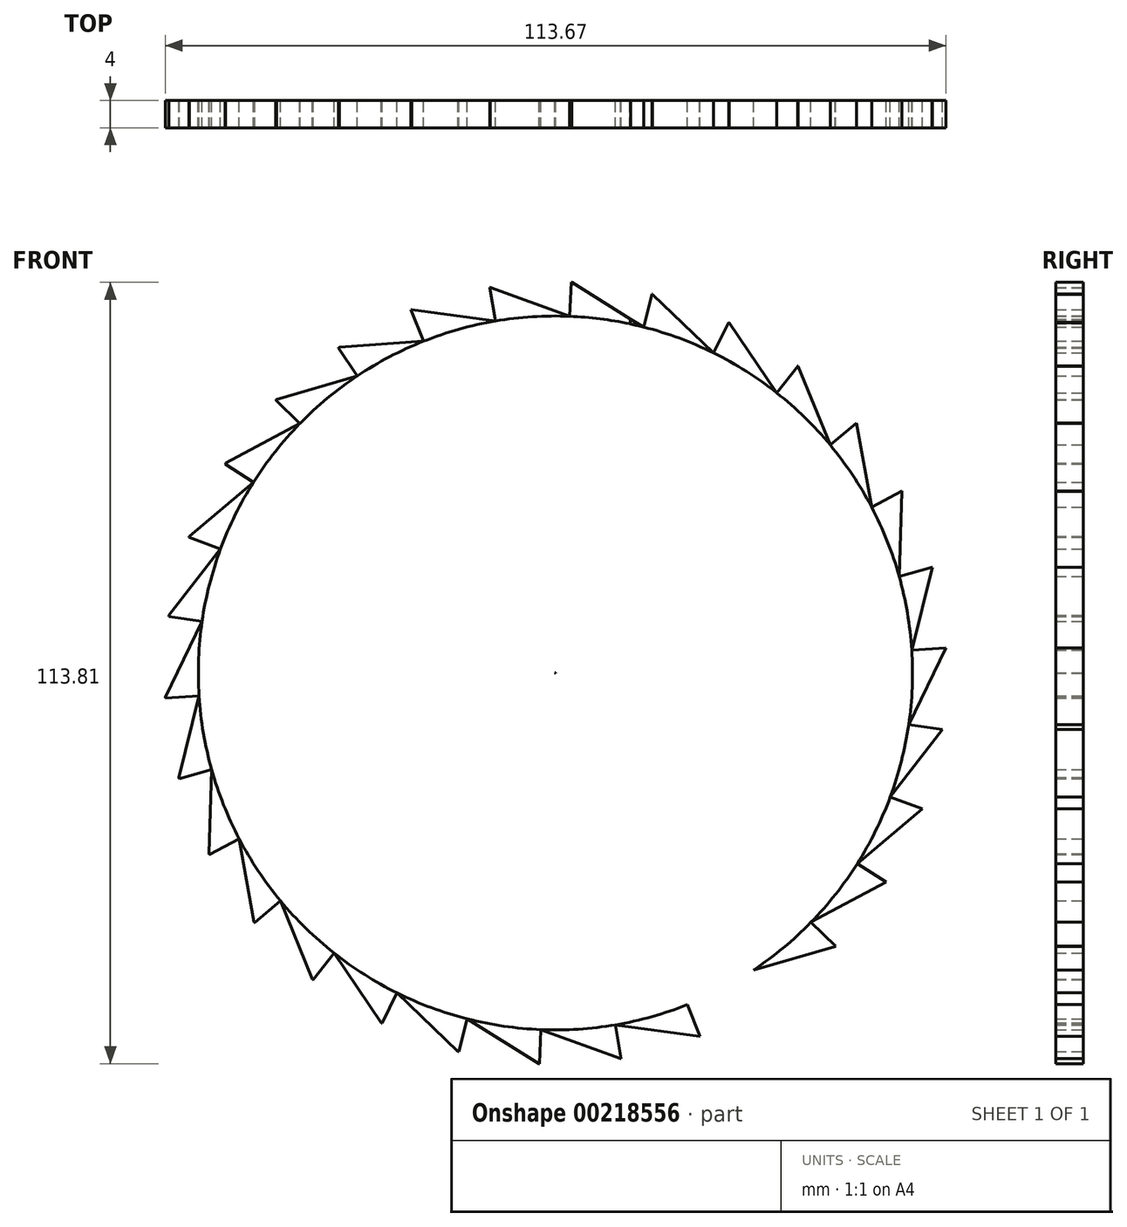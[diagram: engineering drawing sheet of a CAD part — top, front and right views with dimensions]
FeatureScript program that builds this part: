
annotation { "Feature Type Name" : "Feature", "Feature Type Description" : "" }
export const myFeature = defineFeature(function(context is Context, id is Id, definition is map)
    precondition{}
    {
        {
            var Q0;
            Q0=qCreatedBy(makeId("Front.planeOp"),FACE);
            var sketch = newSketch(context, id + "F0", { "sketchPlane" : qUnion([Q0])});
            skLineSegment(sketch, "E0", {"start": v(16.93, -54.43) * mm, "end": v(16.97, -54.42) * mm});
            skPoint(sketch, "E1.center", {"position": v(-0.03, 0) * mm});
            skCircle(sketch, "E2", {"center": v(-0.03, 0) * mm, "radius": 52 * mm});
            skLineSegment(sketch, "E3", {"start": v(0, 0) * mm, "end": v(-0.03, 0) * mm});
            skLineSegment(sketch, "E4", {"start": v(48.74, -18.05) * mm, "end": v(53.43, -19.79) * mm});
            skLineSegment(sketch, "E5", {"start": v(53.43, -19.79) * mm, "end": v(43.92, -27.8) * mm});
            skLineSegment(sketch, "E6.1.0", {"start": v(43.92, -27.8) * mm, "end": v(48.14, -30.47) * mm});
            skLineSegment(sketch, "E6.1.1", {"start": v(48.14, -30.47) * mm, "end": v(37.18, -36.33) * mm});
            skLineSegment(sketch, "E6.2.0", {"start": v(37.18, -36.33) * mm, "end": v(40.76, -39.82) * mm});
            skLineSegment(sketch, "E6.2.1", {"start": v(40.76, -39.82) * mm, "end": v(28.81, -43.27) * mm});
            skLineSegment(sketch, "E6.3.0", {"start": v(28.81, -43.27) * mm, "end": v(31.59, -47.43) * mm});
            skLineSegment(sketch, "E6.3.1", {"start": v(31.59, -47.43) * mm, "end": v(19.18, -48.32) * mm});
            skLineSegment(sketch, "E6.4.0", {"start": v(19.19, -48.32) * mm, "end": v(21.03, -52.96) * mm});
            skLineSegment(sketch, "E6.4.1", {"start": v(21.03, -52.96) * mm, "end": v(8.72, -51.26) * mm});
            skLineSegment(sketch, "E6.5.0", {"start": v(8.72, -51.26) * mm, "end": v(9.56, -56.19) * mm});
            skLineSegment(sketch, "E6.5.1", {"start": v(9.56, -56.19) * mm, "end": v(-2.13, -51.96) * mm});
            skLineSegment(sketch, "E6.6.0", {"start": v(-2.13, -51.96) * mm, "end": v(-2.33, -56.95) * mm});
            skLineSegment(sketch, "E6.6.1", {"start": v(-2.33, -56.95) * mm, "end": v(-12.89, -50.39) * mm});
            skLineSegment(sketch, "E6.7.0", {"start": v(-12.88, -50.39) * mm, "end": v(-14.12, -55.23) * mm});
            skLineSegment(sketch, "E6.7.1", {"start": v(-14.12, -55.23) * mm, "end": v(-23.08, -46.61) * mm});
            skLineSegment(sketch, "E6.8.0", {"start": v(-23.08, -46.61) * mm, "end": v(-25.3, -51.1) * mm});
            skLineSegment(sketch, "E6.8.1", {"start": v(-25.3, -51.1) * mm, "end": v(-32.27, -40.8) * mm});
            skLineSegment(sketch, "E6.9.0", {"start": v(-32.27, -40.8) * mm, "end": v(-35.37, -44.72) * mm});
            skLineSegment(sketch, "E6.9.1", {"start": v(-35.37, -44.72) * mm, "end": v(-40.05, -33.2) * mm});
            skLineSegment(sketch, "E6.10.0", {"start": v(-40.05, -33.2) * mm, "end": v(-43.9, -36.4) * mm});
            skLineSegment(sketch, "E6.10.1", {"start": v(-43.9, -36.4) * mm, "end": v(-46.08, -24.16) * mm});
            skLineSegment(sketch, "E6.11.0", {"start": v(-46.08, -24.16) * mm, "end": v(-50.5, -26.49) * mm});
            skLineSegment(sketch, "E6.11.1", {"start": v(-50.5, -26.49) * mm, "end": v(-50.1, -14.06) * mm});
            skLineSegment(sketch, "E6.12.0", {"start": v(-50.1, -14.06) * mm, "end": v(-54.9, -15.41) * mm});
            skLineSegment(sketch, "E6.12.1", {"start": v(-54.9, -15.41) * mm, "end": v(-51.92, -3.34) * mm});
            skLineSegment(sketch, "E6.13.0", {"start": v(-51.92, -3.34) * mm, "end": v(-56.91, -3.67) * mm});
            skLineSegment(sketch, "E6.13.1", {"start": v(-56.91, -3.67) * mm, "end": v(-51.48, 7.52) * mm});
            skLineSegment(sketch, "E6.14.0", {"start": v(-51.48, 7.52) * mm, "end": v(-56.43, 8.24) * mm});
            skLineSegment(sketch, "E6.14.1", {"start": v(-56.43, 8.24) * mm, "end": v(-48.8, 18.05) * mm});
            skLineSegment(sketch, "E6.15.0", {"start": v(-48.8, 18.05) * mm, "end": v(-53.49, 19.79) * mm});
            skLineSegment(sketch, "E6.15.1", {"start": v(-53.49, 19.79) * mm, "end": v(-43.98, 27.8) * mm});
            skLineSegment(sketch, "E6.16.0", {"start": v(-43.98, 27.8) * mm, "end": v(-48.2, 30.47) * mm});
            skLineSegment(sketch, "E6.16.1", {"start": v(-48.2, 30.47) * mm, "end": v(-37.24, 36.33) * mm});
            skLineSegment(sketch, "E6.17.0", {"start": v(-37.24, 36.33) * mm, "end": v(-40.82, 39.82) * mm});
            skLineSegment(sketch, "E6.17.1", {"start": v(-40.82, 39.82) * mm, "end": v(-28.87, 43.27) * mm});
            skLineSegment(sketch, "E6.18.0", {"start": v(-28.87, 43.27) * mm, "end": v(-31.65, 47.43) * mm});
            skLineSegment(sketch, "E6.18.1", {"start": v(-31.65, 47.43) * mm, "end": v(-19.24, 48.32) * mm});
            skLineSegment(sketch, "E6.19.0", {"start": v(-19.25, 48.32) * mm, "end": v(-21.1, 52.96) * mm});
            skLineSegment(sketch, "E6.19.1", {"start": v(-21.1, 52.96) * mm, "end": v(-8.78, 51.26) * mm});
            skLineSegment(sketch, "E6.20.0", {"start": v(-8.78, 51.26) * mm, "end": v(-9.62, 56.19) * mm});
            skLineSegment(sketch, "E6.20.1", {"start": v(-9.62, 56.19) * mm, "end": v(2.07, 51.96) * mm});
            skLineSegment(sketch, "E6.21.0", {"start": v(2.07, 51.96) * mm, "end": v(2.27, 56.95) * mm});
            skLineSegment(sketch, "E6.21.1", {"start": v(2.27, 56.95) * mm, "end": v(12.83, 50.39) * mm});
            skLineSegment(sketch, "E6.22.0", {"start": v(12.82, 50.39) * mm, "end": v(14.06, 55.23) * mm});
            skLineSegment(sketch, "E6.22.1", {"start": v(14.06, 55.23) * mm, "end": v(23.02, 46.61) * mm});
            skLineSegment(sketch, "E6.23.0", {"start": v(23.02, 46.61) * mm, "end": v(25.24, 51.1) * mm});
            skLineSegment(sketch, "E6.23.1", {"start": v(25.24, 51.1) * mm, "end": v(32.2, 40.8) * mm});
            skLineSegment(sketch, "E6.24.0", {"start": v(32.2, 40.8) * mm, "end": v(35.3, 44.72) * mm});
            skLineSegment(sketch, "E6.24.1", {"start": v(35.3, 44.72) * mm, "end": v(39.99, 33.2) * mm});
            skLineSegment(sketch, "E6.25.0", {"start": v(39.99, 33.2) * mm, "end": v(43.83, 36.4) * mm});
            skLineSegment(sketch, "E6.25.1", {"start": v(43.83, 36.4) * mm, "end": v(46.02, 24.16) * mm});
            skLineSegment(sketch, "E6.26.0", {"start": v(46.02, 24.16) * mm, "end": v(50.44, 26.49) * mm});
            skLineSegment(sketch, "E6.26.1", {"start": v(50.44, 26.49) * mm, "end": v(50.03, 14.06) * mm});
            skLineSegment(sketch, "E6.27.0", {"start": v(50.03, 14.06) * mm, "end": v(54.85, 15.41) * mm});
            skLineSegment(sketch, "E6.27.1", {"start": v(54.85, 15.41) * mm, "end": v(51.86, 3.34) * mm});
            skLineSegment(sketch, "E6.28.0", {"start": v(51.86, 3.34) * mm, "end": v(56.85, 3.67) * mm});
            skLineSegment(sketch, "E6.28.1", {"start": v(56.85, 3.67) * mm, "end": v(51.42, -7.52) * mm});
            skLineSegment(sketch, "E6.29.0", {"start": v(51.42, -7.52) * mm, "end": v(56.37, -8.24) * mm});
            skLineSegment(sketch, "E6.29.1", {"start": v(56.37, -8.24) * mm, "end": v(48.74, -18.05) * mm});
            skLineSegment(sketch, "E7", {"start": v(30.07, -45.16) * mm, "end": v(31.59, -47.43) * mm});
            skPoint(sketch, "E8.visualSharp", {"position": v(33.26, -42.81) * mm});
            skArc(sketch, "E8.filletArc", {"start": v(33.31, -42.89) * mm, "mid": v(33.25, -42.83) * mm, "end": v(33.17, -42.8) * mm});
            skPoint(sketch, "E9.visualSharp", {"position": v(30.65, -45.05) * mm});
            skLineSegment(sketch, "E10", {"start": v(-0.03, 0) * mm, "end": v(0, 0.04) * mm});
            skArc(sketch, "E11", {"start": v(35.3, 44.72) * mm, "mid": v(35.3, 44.73) * mm, "end": v(35.3, 44.73) * mm});
            skLineSegment(sketch, "E12", {"start": v(32.2, 40.8) * mm, "end": v(32.2, 40.82) * mm});
            skLineSegment(sketch, "E13.trimOffspring", {"start": v(32.2, 40.8) * mm, "end": v(35.3, 44.73) * mm});
            skArc(sketch, "E14", {"start": v(-8.23, 38.75) * mm, "mid": v(-28, 28) * mm, "end": v(-38.72, 8.22) * mm});
            skCircle(sketch, "E15", {"center": v(0, 0.04) * mm, "radius": 1.5 * mm});
            skArc(sketch, "E16", {"start": v(-4.9, -1) * mm, "mid": v(-3.54, -3.5) * mm, "end": v(-1.04, -4.85) * mm});
            skLineSegment(sketch, "E17", {"start": v(0, 52) * mm, "end": v(0, 52.7) * mm, "construction": true});
            skLineSegment(sketch, "E18", {"start": v(-1.04, 4.93) * mm, "end": v(-8.23, 38.75) * mm});
            skLineSegment(sketch, "E19", {"start": v(1.04, 4.93) * mm, "end": v(8.23, 38.75) * mm});
            skLineSegment(sketch, "E20.trimOffspring", {"start": v(10.8, 50.86) * mm, "end": v(10.95, 51.55) * mm});
            skPoint(sketch, "E21.orphan", {"position": v(0, 5.04) * mm});
            skLineSegment(sketch, "E22", {"start": v(0, 0.04) * mm, "end": v(0, 0) * mm});
            skLineSegment(sketch, "E23", {"start": v(-38.72, 8.22) * mm, "end": v(-4.9, 1.04) * mm});
            skLineSegment(sketch, "E24", {"start": v(0, 0.04) * mm, "end": v(-0.1, 0.02) * mm});
            skLineSegment(sketch, "E25", {"start": v(0, 0) * mm, "end": v(0, 0) * mm});
            skLineSegment(sketch, "E26.trimOffspring", {"start": v(-0.1, 0.02) * mm, "end": v(0, 0) * mm});
            skLineSegment(sketch, "E27.trimOffspring", {"start": v(-4.9, -1) * mm, "end": v(-38.71, -8.2) * mm});
            skLineSegment(sketch, "E28.trimOffspring", {"start": v(4.9, 1.04) * mm, "end": v(38.72, 8.23) * mm});
            skLineSegment(sketch, "E29.trimOffspring", {"start": v(4.88, -1.04) * mm, "end": v(38.7, -8.23) * mm});
            skLineSegment(sketch, "E30.trimOffspring", {"start": v(1.04, -4.85) * mm, "end": v(8.23, -38.67) * mm});
            skLineSegment(sketch, "E31.trimOffspring", {"start": v(-1.04, -4.85) * mm, "end": v(-8.23, -38.67) * mm});
            skArc(sketch, "E32.trimOffspring", {"start": v(-1.04, 4.93) * mm, "mid": v(-3.55, 3.56) * mm, "end": v(-4.9, 1.04) * mm});
            skArc(sketch, "E33.trimOffspring", {"start": v(4.9, 1.04) * mm, "mid": v(3.55, 3.56) * mm, "end": v(1.04, 4.93) * mm});
            skArc(sketch, "E34.trimOffspring", {"start": v(1.04, -4.85) * mm, "mid": v(3.52, -3.51) * mm, "end": v(4.88, -1.04) * mm});
            skArc(sketch, "E35.trimOffspring", {"start": v(38.72, 8.23) * mm, "mid": v(28, 28.01) * mm, "end": v(8.23, 38.75) * mm});
            skArc(sketch, "E36.trimOffspring", {"start": v(8.23, -38.67) * mm, "mid": v(27.97, -27.96) * mm, "end": v(38.7, -8.23) * mm});
            skArc(sketch, "E37.trimOffspring", {"start": v(-38.71, -8.2) * mm, "mid": v(-27.99, -27.95) * mm, "end": v(-8.23, -38.67) * mm});
            skCircle(sketch, "E38", {"center": v(0, 0) * mm, "radius": 56.95 * mm});
            skSolve(sketch);
        }
        {
            var Q0;
            {var subQ0=sQuery(id+"F0.wireOp",EDGE,"E5");var subQ1=sQuery(id+"F0.wireOp",EDGE,"E2");var subQ2=makeQuery(id+"F0.imprint","INTERSECT",VERTEX,{"derivedFrom":[subQ1,subQ0]});Q0=makeQuery(id+"F0.imprint","IMPRINT",FACE,{"disambiguationData":[TD([[makeQuery(id+"F0.imprint","IMPRINT",EDGE,{"disambiguationData":[TD([[subQ2,1.0]])],"derivedFrom":subQ1}),-1.0]])]});}
            var Q1;
            {var subQ5=sQuery(id+"F0.wireOp",EDGE,"E6.7.1");var subQ7=sQuery(id+"F0.wireOp",EDGE,"E2");var subQ8=makeQuery(id+"F0.imprint","INTERSECT",VERTEX,{"derivedFrom":[subQ7,subQ5]});Q1=makeQuery(id+"F0.imprint","IMPRINT",FACE,{"disambiguationData":[TD([[makeQuery(id+"F0.imprint","IMPRINT",EDGE,{"disambiguationData":[TD([[subQ8,1.0]])],"derivedFrom":subQ7}),-1.0]])]});}
            var Q2;
            {var subQ0=sQuery(id+"F0.wireOp",EDGE,"E7");Q2=makeQuery(id+"F0.imprint","IMPRINT",FACE,{"disambiguationData":[TD([[makeQuery(id+"F0.imprint","IMPRINT",EDGE,{"derivedFrom":subQ0}),-1.0]])]});}
            var Q3;
            {var subQ5=sQuery(id+"F0.wireOp",EDGE,"E6.6.1");var subQ7=sQuery(id+"F0.wireOp",EDGE,"E2");var subQ8=makeQuery(id+"F0.imprint","INTERSECT",VERTEX,{"derivedFrom":[subQ7,subQ5]});Q3=makeQuery(id+"F0.imprint","IMPRINT",FACE,{"disambiguationData":[TD([[makeQuery(id+"F0.imprint","IMPRINT",EDGE,{"disambiguationData":[TD([[subQ8,1.0]])],"derivedFrom":subQ7}),-1.0]])]});}
            var Q4;
            {var subQ5=sQuery(id+"F0.wireOp",EDGE,"E6.8.1");var subQ7=sQuery(id+"F0.wireOp",EDGE,"E2");var subQ8=makeQuery(id+"F0.imprint","INTERSECT",VERTEX,{"derivedFrom":[subQ7,subQ5]});Q4=makeQuery(id+"F0.imprint","IMPRINT",FACE,{"disambiguationData":[TD([[makeQuery(id+"F0.imprint","IMPRINT",EDGE,{"disambiguationData":[TD([[subQ8,1.0]])],"derivedFrom":subQ7}),-1.0]])]});}
            var Q5;
            Q5=makeQuery(id+"F0.imprint","IMPRINT",FACE,{"disambiguationData":[TD([[makeQuery(id+"F0.imprint","IMPRINT",EDGE,{"derivedFrom":sQuery(id+"F0.wireOp",EDGE,"E14")}),-1.0]])]});
            var Q6;
            {var subQ5=sQuery(id+"F0.wireOp",EDGE,"E6.4.1");var subQ7=sQuery(id+"F0.wireOp",EDGE,"E2");var subQ8=makeQuery(id+"F0.imprint","INTERSECT",VERTEX,{"derivedFrom":[subQ7,subQ5]});Q6=makeQuery(id+"F0.imprint","IMPRINT",FACE,{"disambiguationData":[TD([[makeQuery(id+"F0.imprint","IMPRINT",EDGE,{"disambiguationData":[TD([[subQ8,1.0]])],"derivedFrom":subQ7}),-1.0]])]});}
            var Q7;
            {var subQ0=sQuery(id+"F0.wireOp",EDGE,"E6.5.1");var subQ1=sQuery(id+"F0.wireOp",EDGE,"E2");var subQ2=makeQuery(id+"F0.imprint","INTERSECT",VERTEX,{"derivedFrom":[subQ1,subQ0]});Q7=makeQuery(id+"F0.imprint","IMPRINT",FACE,{"disambiguationData":[TD([[makeQuery(id+"F0.imprint","IMPRINT",EDGE,{"disambiguationData":[TD([[subQ2,1.0]])],"derivedFrom":subQ1}),-1.0]])]});}
            var Q8;
            {var subQ0=sQuery(id+"F0.wireOp",EDGE,"E6.3.1");var subQ1=sQuery(id+"F0.wireOp",EDGE,"E2");var subQ2=makeQuery(id+"F0.imprint","INTERSECT",VERTEX,{"derivedFrom":[subQ1,subQ0]});Q8=makeQuery(id+"F0.imprint","IMPRINT",FACE,{"disambiguationData":[TD([[makeQuery(id+"F0.imprint","IMPRINT",EDGE,{"disambiguationData":[TD([[subQ2,1.0]])],"derivedFrom":subQ1}),-1.0]])]});}
            var Q9;
            {var subQ5=sQuery(id+"F0.wireOp",EDGE,"E6.1.1");var subQ7=sQuery(id+"F0.wireOp",EDGE,"E2");var subQ8=makeQuery(id+"F0.imprint","INTERSECT",VERTEX,{"derivedFrom":[subQ7,subQ5]});Q9=makeQuery(id+"F0.imprint","IMPRINT",FACE,{"disambiguationData":[TD([[makeQuery(id+"F0.imprint","IMPRINT",EDGE,{"disambiguationData":[TD([[subQ8,1.0]])],"derivedFrom":subQ7}),-1.0]])]});}
            var Q10;
            {var subQ0=sQuery(id+"F0.wireOp",EDGE,"E6.4.1");var subQ1=sQuery(id+"F0.wireOp",EDGE,"E2");var subQ2=makeQuery(id+"F0.imprint","INTERSECT",VERTEX,{"derivedFrom":[subQ1,subQ0]});Q10=makeQuery(id+"F0.imprint","IMPRINT",FACE,{"disambiguationData":[TD([[makeQuery(id+"F0.imprint","IMPRINT",EDGE,{"disambiguationData":[TD([[subQ2,-1.0]])],"derivedFrom":subQ1}),-1.0]])]});}
            var Q11;
            {var subQ0=sQuery(id+"F0.wireOp",EDGE,"E6.1.1");var subQ1=sQuery(id+"F0.wireOp",EDGE,"E2");var subQ2=makeQuery(id+"F0.imprint","INTERSECT",VERTEX,{"derivedFrom":[subQ1,subQ0]});Q11=makeQuery(id+"F0.imprint","IMPRINT",FACE,{"disambiguationData":[TD([[makeQuery(id+"F0.imprint","IMPRINT",EDGE,{"disambiguationData":[TD([[subQ2,-1.0]])],"derivedFrom":subQ1}),-1.0]])]});}
            var Q12;
            {var subQ0=sQuery(id+"F0.wireOp",EDGE,"E6.3.1");var subQ1=sQuery(id+"F0.wireOp",EDGE,"E2");var subQ2=makeQuery(id+"F0.imprint","INTERSECT",VERTEX,{"derivedFrom":[subQ1,subQ0]});Q12=makeQuery(id+"F0.imprint","IMPRINT",FACE,{"disambiguationData":[TD([[makeQuery(id+"F0.imprint","IMPRINT",EDGE,{"disambiguationData":[TD([[subQ2,-1.0]])],"derivedFrom":subQ1}),-1.0]])]});}
            var Q13;
            {var subQ0=sQuery(id+"F0.wireOp",EDGE,"E6.5.1");var subQ1=sQuery(id+"F0.wireOp",EDGE,"E2");var subQ2=makeQuery(id+"F0.imprint","INTERSECT",VERTEX,{"derivedFrom":[subQ1,subQ0]});Q13=makeQuery(id+"F0.imprint","IMPRINT",FACE,{"disambiguationData":[TD([[makeQuery(id+"F0.imprint","IMPRINT",EDGE,{"disambiguationData":[TD([[subQ2,-1.0]])],"derivedFrom":subQ1}),-1.0]])]});}
            var Q14;
            {var subQ0=sQuery(id+"F0.wireOp",EDGE,"E6.6.1");var subQ1=sQuery(id+"F0.wireOp",EDGE,"E2");var subQ2=makeQuery(id+"F0.imprint","INTERSECT",VERTEX,{"derivedFrom":[subQ1,subQ0]});Q14=makeQuery(id+"F0.imprint","IMPRINT",FACE,{"disambiguationData":[TD([[makeQuery(id+"F0.imprint","IMPRINT",EDGE,{"disambiguationData":[TD([[subQ2,-1.0]])],"derivedFrom":subQ1}),-1.0]])]});}
            var Q15;
            {var subQ0=sQuery(id+"F0.wireOp",EDGE,"E6.8.1");var subQ1=sQuery(id+"F0.wireOp",EDGE,"E2");var subQ2=makeQuery(id+"F0.imprint","INTERSECT",VERTEX,{"derivedFrom":[subQ1,subQ0]});Q15=makeQuery(id+"F0.imprint","IMPRINT",FACE,{"disambiguationData":[TD([[makeQuery(id+"F0.imprint","IMPRINT",EDGE,{"disambiguationData":[TD([[subQ2,-1.0]])],"derivedFrom":subQ1}),-1.0]])]});}
            var Q16;
            {var subQ0=sQuery(id+"F0.wireOp",EDGE,"E6.7.1");var subQ1=sQuery(id+"F0.wireOp",EDGE,"E2");var subQ2=makeQuery(id+"F0.imprint","INTERSECT",VERTEX,{"derivedFrom":[subQ1,subQ0]});Q16=makeQuery(id+"F0.imprint","IMPRINT",FACE,{"disambiguationData":[TD([[makeQuery(id+"F0.imprint","IMPRINT",EDGE,{"disambiguationData":[TD([[subQ2,-1.0]])],"derivedFrom":subQ1}),-1.0]])]});}
            var Q17;
            {var subQ0=sQuery(id+"F0.wireOp",EDGE,"E6.2.1");var subQ1=sQuery(id+"F0.wireOp",EDGE,"E2");var subQ2=makeQuery(id+"F0.imprint","INTERSECT",VERTEX,{"derivedFrom":[subQ1,subQ0]});Q17=makeQuery(id+"F0.imprint","IMPRINT",FACE,{"disambiguationData":[TD([[makeQuery(id+"F0.imprint","IMPRINT",EDGE,{"disambiguationData":[TD([[subQ2,-1.0]])],"derivedFrom":subQ1}),-1.0]])]});}
            var Q18;
            {var subQ5=sQuery(id+"F0.wireOp",EDGE,"E6.25.1");var subQ7=sQuery(id+"F0.wireOp",EDGE,"E2");var subQ8=makeQuery(id+"F0.imprint","INTERSECT",VERTEX,{"derivedFrom":[subQ7,subQ5]});Q18=makeQuery(id+"F0.imprint","IMPRINT",FACE,{"disambiguationData":[TD([[makeQuery(id+"F0.imprint","IMPRINT",EDGE,{"disambiguationData":[TD([[subQ8,1.0]])],"derivedFrom":subQ7}),-1.0]])]});}
            var Q19;
            {var subQ5=sQuery(id+"F0.wireOp",EDGE,"E6.26.1");var subQ6=sQuery(id+"F0.wireOp",EDGE,"E2");var subQ7=makeQuery(id+"F0.imprint","INTERSECT",VERTEX,{"derivedFrom":[subQ6,subQ5]});Q19=makeQuery(id+"F0.imprint","IMPRINT",FACE,{"disambiguationData":[TD([[makeQuery(id+"F0.imprint","IMPRINT",EDGE,{"disambiguationData":[TD([[subQ7,1.0]])],"derivedFrom":subQ6}),-1.0]])]});}
            var Q20;
            {var subQ5=sQuery(id+"F0.wireOp",EDGE,"E4");var subQ6=sQuery(id+"F0.wireOp",EDGE,"E2");var subQ7=makeQuery(id+"F0.imprint","INTERSECT",VERTEX,{"derivedFrom":[subQ6,subQ5]});Q20=makeQuery(id+"F0.imprint","IMPRINT",FACE,{"disambiguationData":[TD([[makeQuery(id+"F0.imprint","IMPRINT",EDGE,{"disambiguationData":[TD([[subQ7,-1.0]])],"derivedFrom":subQ6}),-1.0]])]});}
            var Q21;
            {var subQ5=sQuery(id+"F0.wireOp",EDGE,"E6.24.1");var subQ7=sQuery(id+"F0.wireOp",EDGE,"E2");var subQ8=makeQuery(id+"F0.imprint","INTERSECT",VERTEX,{"derivedFrom":[subQ7,subQ5]});Q21=makeQuery(id+"F0.imprint","IMPRINT",FACE,{"disambiguationData":[TD([[makeQuery(id+"F0.imprint","IMPRINT",EDGE,{"disambiguationData":[TD([[subQ8,1.0]])],"derivedFrom":subQ7}),-1.0]])]});}
            var Q22;
            {var subQ5=sQuery(id+"F0.wireOp",EDGE,"E6.16.1");var subQ7=sQuery(id+"F0.wireOp",EDGE,"E2");var subQ8=makeQuery(id+"F0.imprint","INTERSECT",VERTEX,{"derivedFrom":[subQ7,subQ5]});Q22=makeQuery(id+"F0.imprint","IMPRINT",FACE,{"disambiguationData":[TD([[makeQuery(id+"F0.imprint","IMPRINT",EDGE,{"disambiguationData":[TD([[subQ8,1.0]])],"derivedFrom":subQ7}),-1.0]])]});}
            var Q23;
            {var subQ5=sQuery(id+"F0.wireOp",EDGE,"E6.15.1");var subQ7=sQuery(id+"F0.wireOp",EDGE,"E2");var subQ8=makeQuery(id+"F0.imprint","INTERSECT",VERTEX,{"derivedFrom":[subQ7,subQ5]});Q23=makeQuery(id+"F0.imprint","IMPRINT",FACE,{"disambiguationData":[TD([[makeQuery(id+"F0.imprint","IMPRINT",EDGE,{"disambiguationData":[TD([[subQ8,1.0]])],"derivedFrom":subQ7}),-1.0]])]});}
            var Q24;
            {var subQ0=sQuery(id+"F0.wireOp",EDGE,"E6.25.0");var subQ1=sQuery(id+"F0.wireOp",EDGE,"E2");var subQ2=makeQuery(id+"F0.imprint","INTERSECT",VERTEX,{"derivedFrom":[subQ1,subQ0]});Q24=makeQuery(id+"F0.imprint","IMPRINT",FACE,{"disambiguationData":[TD([[makeQuery(id+"F0.imprint","IMPRINT",EDGE,{"disambiguationData":[TD([[subQ2,-1.0]])],"derivedFrom":subQ0}),1.0]])]});}
            var Q25;
            {var subQ5=sQuery(id+"F0.wireOp",EDGE,"E6.22.1");var subQ7=sQuery(id+"F0.wireOp",EDGE,"E2");var subQ8=makeQuery(id+"F0.imprint","INTERSECT",VERTEX,{"derivedFrom":[subQ7,subQ5]});Q25=makeQuery(id+"F0.imprint","IMPRINT",FACE,{"disambiguationData":[TD([[makeQuery(id+"F0.imprint","IMPRINT",EDGE,{"disambiguationData":[TD([[subQ8,1.0]])],"derivedFrom":subQ7}),-1.0]])]});}
            var Q26;
            {var subQ0=sQuery(id+"F0.wireOp",EDGE,"E6.1.0");var subQ1=sQuery(id+"F0.wireOp",EDGE,"E2");var subQ2=makeQuery(id+"F0.imprint","INTERSECT",VERTEX,{"derivedFrom":[subQ1,subQ0]});Q26=makeQuery(id+"F0.imprint","IMPRINT",FACE,{"disambiguationData":[TD([[makeQuery(id+"F0.imprint","IMPRINT",EDGE,{"disambiguationData":[TD([[subQ2,-1.0]])],"derivedFrom":subQ1}),-1.0]])]});}
            var Q27;
            {var subQ5=sQuery(id+"F0.wireOp",EDGE,"E6.12.1");var subQ7=sQuery(id+"F0.wireOp",EDGE,"E2");var subQ8=makeQuery(id+"F0.imprint","INTERSECT",VERTEX,{"derivedFrom":[subQ7,subQ5]});Q27=makeQuery(id+"F0.imprint","IMPRINT",FACE,{"disambiguationData":[TD([[makeQuery(id+"F0.imprint","IMPRINT",EDGE,{"disambiguationData":[TD([[subQ8,1.0]])],"derivedFrom":subQ7}),-1.0]])]});}
            var Q28;
            {var subQ3=sQuery(id+"F0.wireOp",EDGE,"E20.trimOffspring");Q28=makeQuery(id+"F0.imprint","IMPRINT",FACE,{"disambiguationData":[TD([[makeQuery(id+"F0.imprint","IMPRINT",EDGE,{"derivedFrom":subQ3}),1.0]])]});}
            var Q29;
            {var subQ5=sQuery(id+"F0.wireOp",EDGE,"E6.17.1");var subQ7=sQuery(id+"F0.wireOp",EDGE,"E2");var subQ8=makeQuery(id+"F0.imprint","INTERSECT",VERTEX,{"derivedFrom":[subQ7,subQ5]});Q29=makeQuery(id+"F0.imprint","IMPRINT",FACE,{"disambiguationData":[TD([[makeQuery(id+"F0.imprint","IMPRINT",EDGE,{"disambiguationData":[TD([[subQ8,1.0]])],"derivedFrom":subQ7}),-1.0]])]});}
            var Q30;
            {var subQ5=sQuery(id+"F0.wireOp",EDGE,"E6.13.1");var subQ7=sQuery(id+"F0.wireOp",EDGE,"E2");var subQ8=makeQuery(id+"F0.imprint","INTERSECT",VERTEX,{"derivedFrom":[subQ7,subQ5]});Q30=makeQuery(id+"F0.imprint","IMPRINT",FACE,{"disambiguationData":[TD([[makeQuery(id+"F0.imprint","IMPRINT",EDGE,{"disambiguationData":[TD([[subQ8,1.0]])],"derivedFrom":subQ7}),-1.0]])]});}
            var Q31;
            {var subQ5=sQuery(id+"F0.wireOp",EDGE,"E6.27.1");var subQ7=sQuery(id+"F0.wireOp",EDGE,"E2");var subQ8=makeQuery(id+"F0.imprint","INTERSECT",VERTEX,{"derivedFrom":[subQ7,subQ5]});Q31=makeQuery(id+"F0.imprint","IMPRINT",FACE,{"disambiguationData":[TD([[makeQuery(id+"F0.imprint","IMPRINT",EDGE,{"disambiguationData":[TD([[subQ8,1.0]])],"derivedFrom":subQ7}),-1.0]])]});}
            var Q32;
            {var subQ5=sQuery(id+"F0.wireOp",EDGE,"E6.21.1");var subQ7=sQuery(id+"F0.wireOp",EDGE,"E2");var subQ8=makeQuery(id+"F0.imprint","INTERSECT",VERTEX,{"derivedFrom":[subQ7,subQ5]});Q32=makeQuery(id+"F0.imprint","IMPRINT",FACE,{"disambiguationData":[TD([[makeQuery(id+"F0.imprint","IMPRINT",EDGE,{"disambiguationData":[TD([[subQ8,1.0]])],"derivedFrom":subQ7}),-1.0]])]});}
            var Q33;
            {var subQ5=sQuery(id+"F0.wireOp",EDGE,"E6.9.1");var subQ7=sQuery(id+"F0.wireOp",EDGE,"E2");var subQ8=makeQuery(id+"F0.imprint","INTERSECT",VERTEX,{"derivedFrom":[subQ7,subQ5]});Q33=makeQuery(id+"F0.imprint","IMPRINT",FACE,{"disambiguationData":[TD([[makeQuery(id+"F0.imprint","IMPRINT",EDGE,{"disambiguationData":[TD([[subQ8,1.0]])],"derivedFrom":subQ7}),-1.0]])]});}
            var Q34;
            {var subQ5=sQuery(id+"F0.wireOp",EDGE,"E6.18.1");var subQ7=sQuery(id+"F0.wireOp",EDGE,"E2");var subQ8=makeQuery(id+"F0.imprint","INTERSECT",VERTEX,{"derivedFrom":[subQ7,subQ5]});Q34=makeQuery(id+"F0.imprint","IMPRINT",FACE,{"disambiguationData":[TD([[makeQuery(id+"F0.imprint","IMPRINT",EDGE,{"disambiguationData":[TD([[subQ8,1.0]])],"derivedFrom":subQ7}),-1.0]])]});}
            var Q35;
            {var subQ5=sQuery(id+"F0.wireOp",EDGE,"E6.10.1");var subQ7=sQuery(id+"F0.wireOp",EDGE,"E2");var subQ8=makeQuery(id+"F0.imprint","INTERSECT",VERTEX,{"derivedFrom":[subQ7,subQ5]});Q35=makeQuery(id+"F0.imprint","IMPRINT",FACE,{"disambiguationData":[TD([[makeQuery(id+"F0.imprint","IMPRINT",EDGE,{"disambiguationData":[TD([[subQ8,1.0]])],"derivedFrom":subQ7}),-1.0]])]});}
            var Q36;
            {var subQ5=sQuery(id+"F0.wireOp",EDGE,"E6.14.1");var subQ7=sQuery(id+"F0.wireOp",EDGE,"E2");var subQ8=makeQuery(id+"F0.imprint","INTERSECT",VERTEX,{"derivedFrom":[subQ7,subQ5]});Q36=makeQuery(id+"F0.imprint","IMPRINT",FACE,{"disambiguationData":[TD([[makeQuery(id+"F0.imprint","IMPRINT",EDGE,{"disambiguationData":[TD([[subQ8,1.0]])],"derivedFrom":subQ7}),-1.0]])]});}
            var Q37;
            {var subQ0=sQuery(id+"F0.wireOp",EDGE,"E6.11.1");var subQ1=sQuery(id+"F0.wireOp",EDGE,"E2");var subQ2=makeQuery(id+"F0.imprint","INTERSECT",VERTEX,{"derivedFrom":[subQ1,subQ0]});Q37=makeQuery(id+"F0.imprint","IMPRINT",FACE,{"disambiguationData":[TD([[makeQuery(id+"F0.imprint","IMPRINT",EDGE,{"disambiguationData":[TD([[subQ2,1.0]])],"derivedFrom":subQ1}),-1.0]])]});}
            var Q38;
            {var subQ0=sQuery(id+"F0.wireOp",EDGE,"E6.19.1");var subQ1=sQuery(id+"F0.wireOp",EDGE,"E2");var subQ2=makeQuery(id+"F0.imprint","INTERSECT",VERTEX,{"derivedFrom":[subQ1,subQ0]});Q38=makeQuery(id+"F0.imprint","IMPRINT",FACE,{"disambiguationData":[TD([[makeQuery(id+"F0.imprint","IMPRINT",EDGE,{"disambiguationData":[TD([[subQ2,1.0]])],"derivedFrom":subQ1}),-1.0]])]});}
            var Q39;
            {var subQ0=sQuery(id+"F0.wireOp",EDGE,"E6.12.1");var subQ1=sQuery(id+"F0.wireOp",EDGE,"E2");var subQ2=makeQuery(id+"F0.imprint","INTERSECT",VERTEX,{"derivedFrom":[subQ1,subQ0]});Q39=makeQuery(id+"F0.imprint","IMPRINT",FACE,{"disambiguationData":[TD([[makeQuery(id+"F0.imprint","IMPRINT",EDGE,{"disambiguationData":[TD([[subQ2,-1.0]])],"derivedFrom":subQ1}),-1.0]])]});}
            var Q40;
            {var subQ0=sQuery(id+"F0.wireOp",EDGE,"E6.20.1");var subQ1=sQuery(id+"F0.wireOp",EDGE,"E2");var subQ2=makeQuery(id+"F0.imprint","INTERSECT",VERTEX,{"derivedFrom":[subQ1,subQ0]});Q40=makeQuery(id+"F0.imprint","IMPRINT",FACE,{"disambiguationData":[TD([[makeQuery(id+"F0.imprint","IMPRINT",EDGE,{"disambiguationData":[TD([[subQ2,-1.0]])],"derivedFrom":subQ1}),-1.0]])]});}
            var Q41;
            {var subQ3=sQuery(id+"F0.wireOp",EDGE,"E20.trimOffspring");Q41=makeQuery(id+"F0.imprint","IMPRINT",FACE,{"disambiguationData":[TD([[makeQuery(id+"F0.imprint","IMPRINT",EDGE,{"derivedFrom":subQ3}),-1.0]])]});}
            var Q42;
            {var subQ0=sQuery(id+"F0.wireOp",EDGE,"E6.25.1");var subQ1=sQuery(id+"F0.wireOp",EDGE,"E2");var subQ2=makeQuery(id+"F0.imprint","INTERSECT",VERTEX,{"derivedFrom":[subQ1,subQ0]});Q42=makeQuery(id+"F0.imprint","IMPRINT",FACE,{"disambiguationData":[TD([[makeQuery(id+"F0.imprint","IMPRINT",EDGE,{"disambiguationData":[TD([[subQ2,-1.0]])],"derivedFrom":subQ1}),-1.0]])]});}
            var Q43;
            {var subQ0=sQuery(id+"F0.wireOp",EDGE,"E6.24.1");var subQ1=sQuery(id+"F0.wireOp",EDGE,"E2");var subQ2=makeQuery(id+"F0.imprint","INTERSECT",VERTEX,{"derivedFrom":[subQ1,subQ0]});Q43=makeQuery(id+"F0.imprint","IMPRINT",FACE,{"disambiguationData":[TD([[makeQuery(id+"F0.imprint","IMPRINT",EDGE,{"disambiguationData":[TD([[subQ2,-1.0]])],"derivedFrom":subQ1}),-1.0]])]});}
            var Q44;
            {var subQ0=sQuery(id+"F0.wireOp",EDGE,"E6.26.1");var subQ1=sQuery(id+"F0.wireOp",EDGE,"E2");var subQ2=makeQuery(id+"F0.imprint","INTERSECT",VERTEX,{"derivedFrom":[subQ1,subQ0]});Q44=makeQuery(id+"F0.imprint","IMPRINT",FACE,{"disambiguationData":[TD([[makeQuery(id+"F0.imprint","IMPRINT",EDGE,{"disambiguationData":[TD([[subQ2,-1.0]])],"derivedFrom":subQ1}),-1.0]])]});}
            var Q45;
            {var subQ0=sQuery(id+"F0.wireOp",EDGE,"E6.27.1");var subQ1=sQuery(id+"F0.wireOp",EDGE,"E2");var subQ2=makeQuery(id+"F0.imprint","INTERSECT",VERTEX,{"derivedFrom":[subQ1,subQ0]});Q45=makeQuery(id+"F0.imprint","IMPRINT",FACE,{"disambiguationData":[TD([[makeQuery(id+"F0.imprint","IMPRINT",EDGE,{"disambiguationData":[TD([[subQ2,-1.0]])],"derivedFrom":subQ1}),-1.0]])]});}
            var Q46;
            {var subQ0=sQuery(id+"F0.wireOp",EDGE,"E6.9.1");var subQ1=sQuery(id+"F0.wireOp",EDGE,"E2");var subQ2=makeQuery(id+"F0.imprint","INTERSECT",VERTEX,{"derivedFrom":[subQ1,subQ0]});Q46=makeQuery(id+"F0.imprint","IMPRINT",FACE,{"disambiguationData":[TD([[makeQuery(id+"F0.imprint","IMPRINT",EDGE,{"disambiguationData":[TD([[subQ2,-1.0]])],"derivedFrom":subQ1}),-1.0]])]});}
            var Q47;
            {var subQ0=sQuery(id+"F0.wireOp",EDGE,"E4");var subQ1=sQuery(id+"F0.wireOp",EDGE,"E2");var subQ2=makeQuery(id+"F0.imprint","INTERSECT",VERTEX,{"derivedFrom":[subQ1,subQ0]});Q47=makeQuery(id+"F0.imprint","IMPRINT",FACE,{"disambiguationData":[TD([[makeQuery(id+"F0.imprint","IMPRINT",EDGE,{"disambiguationData":[TD([[subQ2,1.0]])],"derivedFrom":subQ1}),-1.0]])]});}
            var Q48;
            {var subQ0=sQuery(id+"F0.wireOp",EDGE,"E6.22.1");var subQ1=sQuery(id+"F0.wireOp",EDGE,"E2");var subQ2=makeQuery(id+"F0.imprint","INTERSECT",VERTEX,{"derivedFrom":[subQ1,subQ0]});Q48=makeQuery(id+"F0.imprint","IMPRINT",FACE,{"disambiguationData":[TD([[makeQuery(id+"F0.imprint","IMPRINT",EDGE,{"disambiguationData":[TD([[subQ2,-1.0]])],"derivedFrom":subQ1}),-1.0]])]});}
            var Q49;
            {var subQ0=sQuery(id+"F0.wireOp",EDGE,"E6.19.1");var subQ1=sQuery(id+"F0.wireOp",EDGE,"E2");var subQ2=makeQuery(id+"F0.imprint","INTERSECT",VERTEX,{"derivedFrom":[subQ1,subQ0]});Q49=makeQuery(id+"F0.imprint","IMPRINT",FACE,{"disambiguationData":[TD([[makeQuery(id+"F0.imprint","IMPRINT",EDGE,{"disambiguationData":[TD([[subQ2,-1.0]])],"derivedFrom":subQ1}),-1.0]])]});}
            var Q50;
            {var subQ0=sQuery(id+"F0.wireOp",EDGE,"E6.11.1");var subQ1=sQuery(id+"F0.wireOp",EDGE,"E2");var subQ2=makeQuery(id+"F0.imprint","INTERSECT",VERTEX,{"derivedFrom":[subQ1,subQ0]});Q50=makeQuery(id+"F0.imprint","IMPRINT",FACE,{"disambiguationData":[TD([[makeQuery(id+"F0.imprint","IMPRINT",EDGE,{"disambiguationData":[TD([[subQ2,-1.0]])],"derivedFrom":subQ1}),-1.0]])]});}
            var Q51;
            {var subQ0=sQuery(id+"F0.wireOp",EDGE,"E6.13.1");var subQ1=sQuery(id+"F0.wireOp",EDGE,"E2");var subQ2=makeQuery(id+"F0.imprint","INTERSECT",VERTEX,{"derivedFrom":[subQ1,subQ0]});Q51=makeQuery(id+"F0.imprint","IMPRINT",FACE,{"disambiguationData":[TD([[makeQuery(id+"F0.imprint","IMPRINT",EDGE,{"disambiguationData":[TD([[subQ2,-1.0]])],"derivedFrom":subQ1}),-1.0]])]});}
            var Q52;
            {var subQ0=sQuery(id+"F0.wireOp",EDGE,"E6.18.1");var subQ1=sQuery(id+"F0.wireOp",EDGE,"E2");var subQ2=makeQuery(id+"F0.imprint","INTERSECT",VERTEX,{"derivedFrom":[subQ1,subQ0]});Q52=makeQuery(id+"F0.imprint","IMPRINT",FACE,{"disambiguationData":[TD([[makeQuery(id+"F0.imprint","IMPRINT",EDGE,{"disambiguationData":[TD([[subQ2,-1.0]])],"derivedFrom":subQ1}),-1.0]])]});}
            var Q53;
            {var subQ0=sQuery(id+"F0.wireOp",EDGE,"E6.21.1");var subQ1=sQuery(id+"F0.wireOp",EDGE,"E2");var subQ2=makeQuery(id+"F0.imprint","INTERSECT",VERTEX,{"derivedFrom":[subQ1,subQ0]});Q53=makeQuery(id+"F0.imprint","IMPRINT",FACE,{"disambiguationData":[TD([[makeQuery(id+"F0.imprint","IMPRINT",EDGE,{"disambiguationData":[TD([[subQ2,-1.0]])],"derivedFrom":subQ1}),-1.0]])]});}
            var Q54;
            {var subQ0=sQuery(id+"F0.wireOp",EDGE,"E6.14.1");var subQ1=sQuery(id+"F0.wireOp",EDGE,"E2");var subQ2=makeQuery(id+"F0.imprint","INTERSECT",VERTEX,{"derivedFrom":[subQ1,subQ0]});Q54=makeQuery(id+"F0.imprint","IMPRINT",FACE,{"disambiguationData":[TD([[makeQuery(id+"F0.imprint","IMPRINT",EDGE,{"disambiguationData":[TD([[subQ2,-1.0]])],"derivedFrom":subQ1}),-1.0]])]});}
            var Q55;
            {var subQ0=sQuery(id+"F0.wireOp",EDGE,"E6.28.1");var subQ1=sQuery(id+"F0.wireOp",EDGE,"E2");var subQ2=makeQuery(id+"F0.imprint","INTERSECT",VERTEX,{"derivedFrom":[subQ1,subQ0]});Q55=makeQuery(id+"F0.imprint","IMPRINT",FACE,{"disambiguationData":[TD([[makeQuery(id+"F0.imprint","IMPRINT",EDGE,{"disambiguationData":[TD([[subQ2,-1.0]])],"derivedFrom":subQ1}),-1.0]])]});}
            var Q56;
            {var subQ0=sQuery(id+"F0.wireOp",EDGE,"E6.17.1");var subQ1=sQuery(id+"F0.wireOp",EDGE,"E2");var subQ2=makeQuery(id+"F0.imprint","INTERSECT",VERTEX,{"derivedFrom":[subQ1,subQ0]});Q56=makeQuery(id+"F0.imprint","IMPRINT",FACE,{"disambiguationData":[TD([[makeQuery(id+"F0.imprint","IMPRINT",EDGE,{"disambiguationData":[TD([[subQ2,-1.0]])],"derivedFrom":subQ1}),-1.0]])]});}
            var Q57;
            {var subQ0=sQuery(id+"F0.wireOp",EDGE,"E6.10.1");var subQ1=sQuery(id+"F0.wireOp",EDGE,"E2");var subQ2=makeQuery(id+"F0.imprint","INTERSECT",VERTEX,{"derivedFrom":[subQ1,subQ0]});Q57=makeQuery(id+"F0.imprint","IMPRINT",FACE,{"disambiguationData":[TD([[makeQuery(id+"F0.imprint","IMPRINT",EDGE,{"disambiguationData":[TD([[subQ2,-1.0]])],"derivedFrom":subQ1}),-1.0]])]});}
            var Q58;
            {var subQ0=sQuery(id+"F0.wireOp",EDGE,"E6.16.1");var subQ1=sQuery(id+"F0.wireOp",EDGE,"E2");var subQ2=makeQuery(id+"F0.imprint","INTERSECT",VERTEX,{"derivedFrom":[subQ1,subQ0]});Q58=makeQuery(id+"F0.imprint","IMPRINT",FACE,{"disambiguationData":[TD([[makeQuery(id+"F0.imprint","IMPRINT",EDGE,{"disambiguationData":[TD([[subQ2,-1.0]])],"derivedFrom":subQ1}),-1.0]])]});}
            var Q59;
            {var subQ0=sQuery(id+"F0.wireOp",EDGE,"E5");var subQ1=sQuery(id+"F0.wireOp",EDGE,"E2");var subQ2=makeQuery(id+"F0.imprint","INTERSECT",VERTEX,{"derivedFrom":[subQ1,subQ0]});Q59=makeQuery(id+"F0.imprint","IMPRINT",FACE,{"disambiguationData":[TD([[makeQuery(id+"F0.imprint","IMPRINT",EDGE,{"disambiguationData":[TD([[subQ2,-1.0]])],"derivedFrom":subQ1}),-1.0]])]});}
            var Q60;
            {var subQ0=sQuery(id+"F0.wireOp",EDGE,"E6.15.1");var subQ1=sQuery(id+"F0.wireOp",EDGE,"E2");var subQ2=makeQuery(id+"F0.imprint","INTERSECT",VERTEX,{"derivedFrom":[subQ1,subQ0]});Q60=makeQuery(id+"F0.imprint","IMPRINT",FACE,{"disambiguationData":[TD([[makeQuery(id+"F0.imprint","IMPRINT",EDGE,{"disambiguationData":[TD([[subQ2,-1.0]])],"derivedFrom":subQ1}),-1.0]])]});}
            var Q61;
            {var subQ0=sQuery(id+"F0.wireOp",EDGE,"E13.trimOffspring");var subQ1=sQuery(id+"F0.wireOp",EDGE,"E6.23.1");var subQ2=makeQuery(id+"F0.imprint","INTERSECT",VERTEX,{"derivedFrom":[subQ1,subQ0]});Q61=makeQuery(id+"F0.imprint","IMPRINT",FACE,{"disambiguationData":[TD([[makeQuery(id+"F0.imprint","IMPRINT",EDGE,{"disambiguationData":[TD([[subQ2,-1.0]])],"derivedFrom":subQ1}),1.0]])]});}
            var Q62;
            {var subQ0=sQuery(id+"F0.wireOp",EDGE,"E11");Q62=makeQuery(id+"F0.imprint","IMPRINT",FACE,{"disambiguationData":[TD([[makeQuery(id+"F0.imprint","IMPRINT",EDGE,{"derivedFrom":subQ0}),1.0]])]});}
            var Q63;
            {var subQ1=sQuery(id+"F0.wireOp",EDGE,"E2");var subQ3=sQuery(id+"F0.wireOp",EDGE,"E6.24.0");var subQ4=makeQuery(id+"F0.imprint","INTERSECT",VERTEX,{"derivedFrom":[subQ1,subQ3]});Q63=makeQuery(id+"F0.imprint","IMPRINT",FACE,{"disambiguationData":[TD([[makeQuery(id+"F0.imprint","IMPRINT",EDGE,{"disambiguationData":[TD([[subQ4,-1.0]])],"derivedFrom":subQ3}),-1.0]])]});}
            var Q64;
            {var subQ1=sQuery(id+"F0.wireOp",EDGE,"E6.23.1");var subQ3=sQuery(id+"F0.wireOp",EDGE,"E6.24.0");var subQ4=makeQuery(id+"F0.imprint","INTERSECT",VERTEX,{"derivedFrom":[subQ1,subQ3]});Q64=makeQuery(id+"F0.imprint","IMPRINT",FACE,{"disambiguationData":[TD([[makeQuery(id+"F0.imprint","IMPRINT",EDGE,{"disambiguationData":[TD([[subQ4,-1.0]])],"derivedFrom":subQ3}),-1.0]])]});}
            var Q65;
            {var subQ0=sQuery(id+"F0.wireOp",EDGE,"E6.24.0");var subQ1=sQuery(id+"F0.wireOp",EDGE,"E2");var subQ2=makeQuery(id+"F0.imprint","INTERSECT",VERTEX,{"derivedFrom":[subQ1,subQ0]});Q65=makeQuery(id+"F0.imprint","IMPRINT",FACE,{"disambiguationData":[TD([[makeQuery(id+"F0.imprint","IMPRINT",EDGE,{"disambiguationData":[TD([[subQ2,-1.0]])],"derivedFrom":subQ1}),-1.0]])]});}
            var Q66;
            {var subQ0=sQuery(id+"F0.wireOp",EDGE,"E25");Q66=makeQuery(id+"F0.imprint","IMPRINT",FACE,{"disambiguationData":[TD([[makeQuery(id+"F0.imprint","IMPRINT",EDGE,{"derivedFrom":subQ0}),1.0]])]});}
            var Q67;
            {var subQ5=sQuery(id+"F0.wireOp",EDGE,"E25");Q67=makeQuery(id+"F0.imprint","IMPRINT",FACE,{"disambiguationData":[TD([[makeQuery(id+"F0.imprint","IMPRINT",EDGE,{"derivedFrom":subQ5}),-1.0]])]});}
            var Q68;
            {var subQ0=sQuery(id+"F0.wireOp",EDGE,"E10");Q68=makeQuery(id+"F0.imprint","IMPRINT",FACE,{"disambiguationData":[TD([[makeQuery(id+"F0.imprint","IMPRINT",EDGE,{"derivedFrom":subQ0}),-1.0]])]});}
            var Q69;
            {var subQ0=sQuery(id+"F0.wireOp",EDGE,"E26.trimOffspring");var subQ3=sQuery(id+"F0.wireOp",EDGE,"E22");var subQ5=makeQuery(id+"F0.imprint","INTERSECT",VERTEX,{"derivedFrom":[subQ3,subQ0]});Q69=makeQuery(id+"F0.imprint","IMPRINT",FACE,{"disambiguationData":[TD([[makeQuery(id+"F0.imprint","IMPRINT",EDGE,{"disambiguationData":[TD([[subQ5,1.0]])],"derivedFrom":subQ3}),-1.0]])]});}
            var Q70;
            {var subQ0=sQuery(id+"F0.wireOp",EDGE,"E10");Q70=makeQuery(id+"F0.imprint","IMPRINT",FACE,{"disambiguationData":[TD([[makeQuery(id+"F0.imprint","IMPRINT",EDGE,{"derivedFrom":subQ0}),1.0]])]});}
            extrude(context, id + "F1", {"entities" : qUnion([Q0, Q1, Q2, Q3, Q4, Q5, Q6, Q7, Q8, Q9, Q10, Q11, Q12, Q13, Q14, Q15, Q16, Q17, Q18, Q19, Q20, Q21, Q22, Q23, Q24, Q25, Q26, Q27, Q28, Q29, Q30, Q31, Q32, Q33, Q34, Q35, Q36, Q37, Q38, Q39, Q40, Q41, Q42, Q43, Q44, Q45, Q46, Q47, Q48, Q49, Q50, Q51, Q52, Q53, Q54, Q55, Q56, Q57, Q58, Q59, Q60, Q61, Q62, Q63, Q64, Q65, Q66, Q67, Q68, Q69, Q70]), "depth" : 4 * mm});
        }
    });
